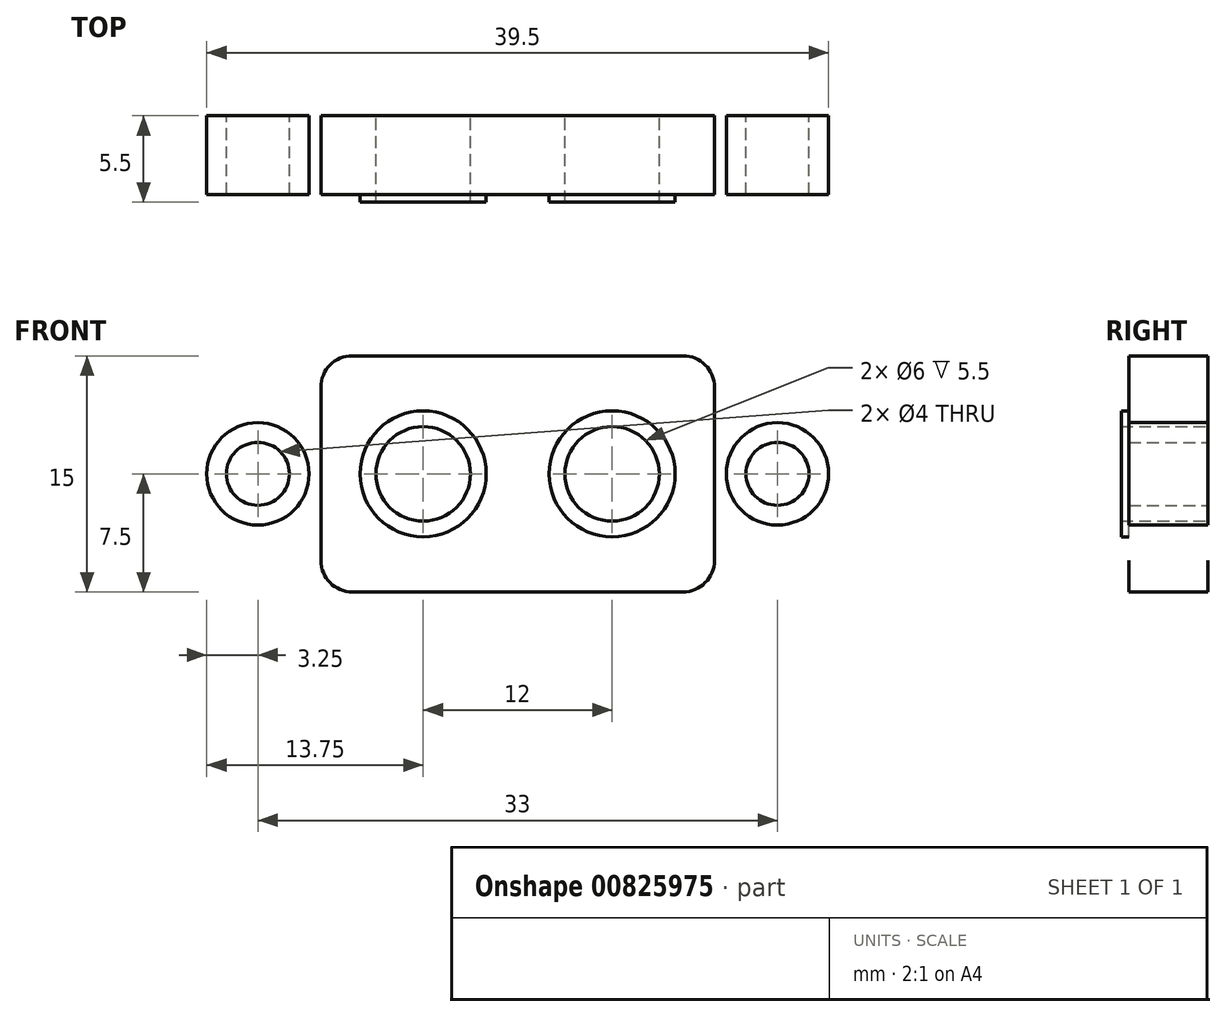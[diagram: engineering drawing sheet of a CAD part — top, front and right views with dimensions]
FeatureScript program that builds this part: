
annotation { "Feature Type Name" : "Feature", "Feature Type Description" : "" }
export const myFeature = defineFeature(function(context is Context, id is Id, definition is map)
    precondition{}
    {
        {
            var Q0;
            Q0=qCreatedBy(makeId("Front.planeOp"),FACE);
            var sketch = newSketch(context, id + "F0", { "sketchPlane" : qUnion([Q0])});
            skPoint(sketch, "E0.middle", {"position": v(0, 0) * mm});
            skLineSegment(sketch, "E1.bottom", {"start": v(10.5, -7.5) * mm, "end": v(-10.5, -7.5) * mm});
            skLineSegment(sketch, "E1.top", {"start": v(10.5, 7.5) * mm, "end": v(-10.5, 7.5) * mm});
            skLineSegment(sketch, "E1.left", {"start": v(12.5, -5.5) * mm, "end": v(12.5, 5.5) * mm});
            skLineSegment(sketch, "E1.right", {"start": v(-12.5, -5.5) * mm, "end": v(-12.5, 5.5) * mm});
            skPoint(sketch, "E2.visualSharp", {"position": v(-12.5, -7.5) * mm});
            skArc(sketch, "E2.filletArc", {"start": v(-12.5, -5.5) * mm, "mid": v(-11.91, -6.91) * mm, "end": v(-10.5, -7.5) * mm});
            skPoint(sketch, "E3.visualSharp", {"position": v(-12.5, 7.5) * mm});
            skArc(sketch, "E3.filletArc", {"start": v(-10.5, 7.5) * mm, "mid": v(-11.91, 6.91) * mm, "end": v(-12.5, 5.5) * mm});
            skPoint(sketch, "E4.visualSharp", {"position": v(12.5, -7.5) * mm});
            skArc(sketch, "E4.filletArc", {"start": v(10.5, -7.5) * mm, "mid": v(11.91, -6.91) * mm, "end": v(12.5, -5.5) * mm});
            skPoint(sketch, "E5.visualSharp", {"position": v(12.5, 7.5) * mm});
            skArc(sketch, "E5.filletArc", {"start": v(12.5, 5.5) * mm, "mid": v(11.91, 6.91) * mm, "end": v(10.5, 7.5) * mm});
            skCircle(sketch, "E6", {"center": v(-6, 0) * mm, "radius": 3 * mm});
            skCircle(sketch, "E7", {"center": v(6, 0) * mm, "radius": 3 * mm});
            skLineSegment(sketch, "E8.bottom", {"start": v(-12.5, 2) * mm, "end": v(-14.2, 2) * mm});
            skLineSegment(sketch, "E8.top", {"start": v(-12.5, -2) * mm, "end": v(-14.2, -2) * mm});
            skLineSegment(sketch, "E8.left", {"start": v(-12.5, 2) * mm, "end": v(-12.5, -2) * mm});
            skLineSegment(sketch, "E8.right", {"start": v(-14.2, 2) * mm, "end": v(-14.2, -2) * mm});
            skPoint(sketch, "E8.middle", {"position": v(-13.35, 0) * mm});
            skPoint(sketch, "E8.middle.positionSnap0", {"position": v(-12.5, 0) * mm});
            skPoint(sketch, "E8.centerSnap0", {"position": v(-12.5, 0) * mm});
            skLineSegment(sketch, "E9.bottom", {"start": v(12.5, 2) * mm, "end": v(14.2, 2) * mm});
            skLineSegment(sketch, "E9.top", {"start": v(12.5, -2) * mm, "end": v(14.2, -2) * mm});
            skLineSegment(sketch, "E9.left", {"start": v(12.5, 2) * mm, "end": v(12.5, -2) * mm});
            skLineSegment(sketch, "E9.right", {"start": v(14.2, 2) * mm, "end": v(14.2, -2) * mm});
            skPoint(sketch, "E9.middle", {"position": v(13.35, 0) * mm});
            skCircle(sketch, "E10", {"center": v(-16.5, 0) * mm, "radius": 3.25 * mm});
            skCircle(sketch, "E11", {"center": v(-16.5, 0) * mm, "radius": 2 * mm});
            skCircle(sketch, "E12", {"center": v(16.5, 0) * mm, "radius": 3.25 * mm});
            skCircle(sketch, "E13", {"center": v(16.5, 0) * mm, "radius": 2 * mm});
            skCircle(sketch, "E14", {"center": v(-6, 0) * mm, "radius": 4 * mm});
            skCircle(sketch, "E15", {"center": v(6, 0) * mm, "radius": 4 * mm});
            skSolve(sketch);
        }
        {
            var Q0;
            {var subQ5=sQuery(id+"F0.wireOp",EDGE,"E9.right");Q0=makeQuery(id+"F0.imprint","IMPRINT",FACE,{"disambiguationData":[TD([[makeQuery(id+"F0.imprint","IMPRINT",EDGE,{"derivedFrom":subQ5}),1.0]])]});}
            var Q1;
            {var subQ0=sQuery(id+"F0.wireOp",EDGE,"E9.right");Q1=makeQuery(id+"F0.imprint","IMPRINT",FACE,{"disambiguationData":[TD([[makeQuery(id+"F0.imprint","IMPRINT",EDGE,{"derivedFrom":subQ0}),-1.0]])]});}
            var Q2;
            {var subQ0=sQuery(id+"F0.wireOp",EDGE,"E9.left");Q2=makeQuery(id+"F0.imprint","IMPRINT",FACE,{"disambiguationData":[TD([[makeQuery(id+"F0.imprint","IMPRINT",EDGE,{"derivedFrom":subQ0}),1.0]])]});}
            var Q3;
            {var subQ5=sQuery(id+"F0.wireOp",EDGE,"E8.right");Q3=makeQuery(id+"F0.imprint","IMPRINT",FACE,{"disambiguationData":[TD([[makeQuery(id+"F0.imprint","IMPRINT",EDGE,{"derivedFrom":subQ5}),-1.0]])]});}
            var Q4;
            {var subQ0=sQuery(id+"F0.wireOp",EDGE,"E8.right");Q4=makeQuery(id+"F0.imprint","IMPRINT",FACE,{"disambiguationData":[TD([[makeQuery(id+"F0.imprint","IMPRINT",EDGE,{"derivedFrom":subQ0}),1.0]])]});}
            var Q5;
            {var subQ0=sQuery(id+"F0.wireOp",EDGE,"E8.left");Q5=makeQuery(id+"F0.imprint","IMPRINT",FACE,{"disambiguationData":[TD([[makeQuery(id+"F0.imprint","IMPRINT",EDGE,{"derivedFrom":subQ0}),-1.0]])]});}
            var Q6;
            Q6=makeQuery(id+"F0.imprint","IMPRINT",FACE,{"disambiguationData":[TD([[makeQuery(id+"F0.imprint","IMPRINT",EDGE,{"derivedFrom":sQuery(id+"F0.wireOp",EDGE,"E1.bottom")}),-1.0]])]});
            extrude(context, id + "F1", {"entities" : qUnion([Q0, Q1, Q2, Q3, Q4, Q5, Q6]), "depth" : 5 * mm, "offsetDistance" : 25 * mm});
        }
        {
            var Q0;
            Q0=makeQuery(id+"F0.imprint","IMPRINT",FACE,{"disambiguationData":[TD([[makeQuery(id+"F0.imprint","IMPRINT",EDGE,{"derivedFrom":sQuery(id+"F0.wireOp",EDGE,"E6")}),-1.0]])]});
            var Q1;
            Q1=makeQuery(id+"F0.imprint","IMPRINT",FACE,{"disambiguationData":[TD([[makeQuery(id+"F0.imprint","IMPRINT",EDGE,{"derivedFrom":sQuery(id+"F0.wireOp",EDGE,"E7")}),-1.0]])]});
            extrude(context, id + "F2", {"entities" : qUnion([Q0, Q1]), "operationType" : NewBodyOperationType.ADD, "depth" : 5.5 * mm, "offsetDistance" : 25 * mm});
        }
    });
